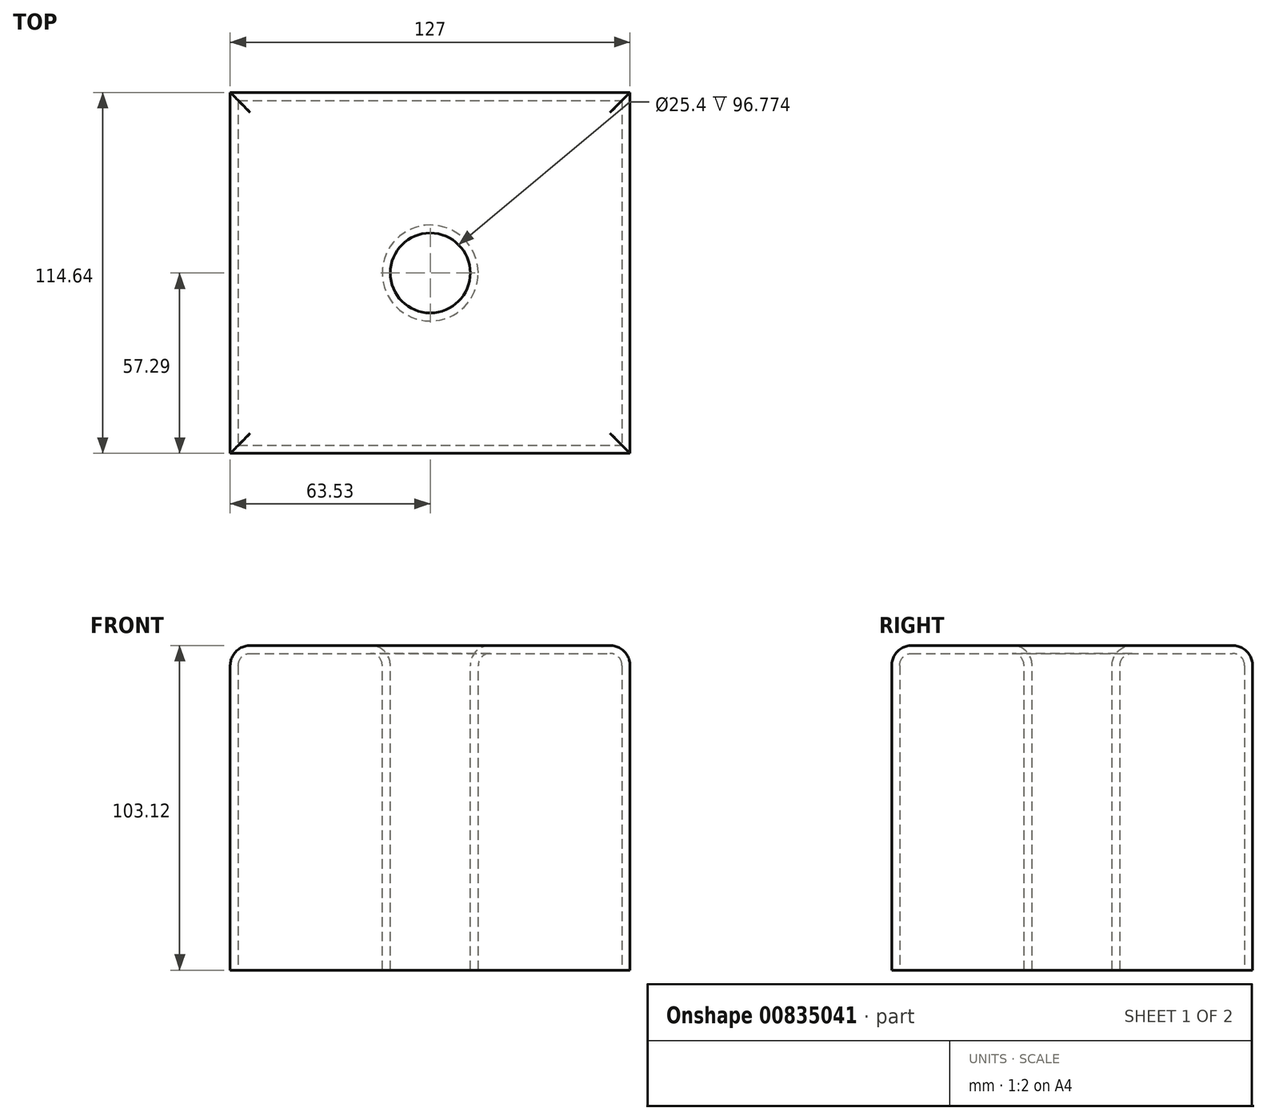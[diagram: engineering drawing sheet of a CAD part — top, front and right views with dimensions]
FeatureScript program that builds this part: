
annotation { "Feature Type Name" : "Feature", "Feature Type Description" : "" }
export const myFeature = defineFeature(function(context is Context, id is Id, definition is map)
    precondition{}
    {
        {
            var Q0;
            Q0=qCreatedBy(makeId("Top.planeOp"),FACE);
            var sketch = newSketch(context, id + "F0", { "sketchPlane" : qUnion([Q0])});
            skLineSegment(sketch, "E0.bottom", {"start": v(-63.53, 57.35) * mm, "end": v(63.47, 57.35) * mm});
            skLineSegment(sketch, "E0.top", {"start": v(-63.53, -57.29) * mm, "end": v(63.47, -57.29) * mm});
            skLineSegment(sketch, "E0.left", {"start": v(-63.53, 57.35) * mm, "end": v(-63.53, -57.29) * mm});
            skLineSegment(sketch, "E0.right", {"start": v(63.47, 57.35) * mm, "end": v(63.47, -57.29) * mm});
            skLineSegment(sketch, "E1", {"start": v(-63.53, 57.35) * mm, "end": v(63.47, -57.29) * mm, "construction": true});
            skLineSegment(sketch, "E2", {"start": v(-63.53, -57.29) * mm, "end": v(63.47, 57.35) * mm, "construction": true});
            skSolve(sketch);
        }
        {
            var Q0;
            Q0 = qSketchRegion(id + "F0", true);
            extrude(context, id + "F1", {"entities" : qUnion([Q0]), "depth" : 103.12 * mm, "offsetDistance" : 25.4 * mm});
        }
        {
            var Q0;
            Q0=makeQuery(id+"F1.opExtrude","CAP_FACE",FACE,{"disambiguationData":[OSD([sQuery(id+"F0.wireOp",EDGE,"E0.bottom"),sQuery(id+"F0.wireOp",EDGE,"E0.top"),sQuery(id+"F0.wireOp",EDGE,"E0.left"),sQuery(id+"F0.wireOp",EDGE,"E0.right")])],"isStart":false});
            var sketch = newSketch(context, id + "F2", { "sketchPlane" : qUnion([Q0])});
            skPoint(sketch, "E3", {"position": v(0, 0) * mm});
            skSolve(sketch);
        }
        {
            var Q0;
            Q0=sQuery(id+"F2.wireOp",VERTEX,"E3");
            var Q1;
            Q1=makeQuery(id+"F1.opExtrude","SWEPT_BODY",BODY,{"disambiguationData":[OSD([sQuery(id+"F0.wireOp",EDGE,"E0.bottom"),sQuery(id+"F0.wireOp",EDGE,"E0.top"),sQuery(id+"F0.wireOp",EDGE,"E0.left"),sQuery(id+"F0.wireOp",EDGE,"E0.right")])]});
            hole(context, id + "F3", {"style" : HoleStyle.SIMPLE, "endStyle" : HoleEndStyle.THROUGH, "holeDiameter" : 25.4 * mm, "majorDiameter" : 6.35 * mm, "isTappedThrough" : true, "tappedDepth" : 12.7 * mm, "tapClearance" : 3, "locations" : qUnion([Q0]), "scope" : qUnion([Q1])});
        }
        {
            var Q0;
            Q0=makeQuery(id+"F1.opExtrude","CAP_FACE",FACE,{"disambiguationData":[OSD([sQuery(id+"F0.wireOp",EDGE,"E0.bottom"),sQuery(id+"F0.wireOp",EDGE,"E0.top"),sQuery(id+"F0.wireOp",EDGE,"E0.left"),sQuery(id+"F0.wireOp",EDGE,"E0.right")])],"isStart":false});
            fillet(context, id + "F4", {"entities" : qUnion([Q0]), "radius" : 6.35 * mm, "tangentPropagation" : true, "allowEdgeOverflow" : false});
        }
        {
            var Q0;
            Q0=makeQuery(id+"F1.opExtrude","CAP_FACE",FACE,{"disambiguationData":[OSD([sQuery(id+"F0.wireOp",EDGE,"E0.bottom"),sQuery(id+"F0.wireOp",EDGE,"E0.top"),sQuery(id+"F0.wireOp",EDGE,"E0.left"),sQuery(id+"F0.wireOp",EDGE,"E0.right")])],"isStart":true});
            shell(context, id + "F5", {"entities" : qUnion([Q0]), "thickness" : 2.54 * mm});
        }
    });
